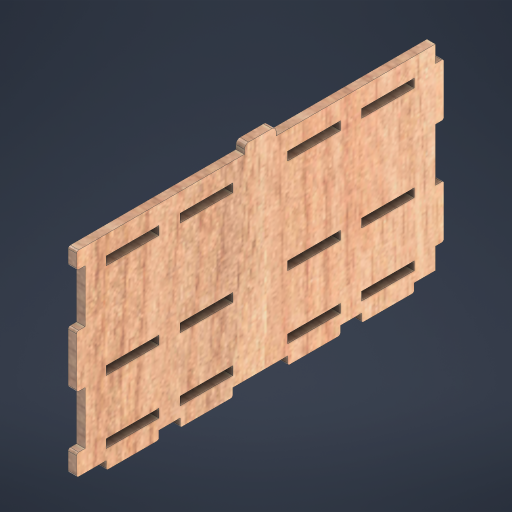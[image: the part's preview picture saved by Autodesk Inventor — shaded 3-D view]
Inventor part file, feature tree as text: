
AUTODESK INVENTOR PART (.ipt)
format: ipt  version: 2024.1 (Build 281209000, 209)  size: 609,792 bytes
history: native  units: mm
features: extrude x1, fillet x1, sketch x1
ambient origin geometry x8: Origin, YZ Plane, XZ Plane, XY Plane, X Axis, Y Axis, Z Axis, Center Point
bodies: Solid1 (feature_tree)
feature tree (3):
  extrude  "Extrusion1"  Depth=25.0mm
  fillet  "Fillet1"  Radius=25.0mm
  sketch  "Sketch1"  dims[d0=4.0mm d1=25.0mm d2=25.0mm d3=10.0mm d4=4.0mm d5=13.0mm d14=75.0mm d15=20.0mm d17=75.0mm d18=10.0mm d20=10.0mm d22=20.0mm d24=45.0mm d25=10.0mm d27=10.0mm d29=9.0mm d30=5.0mm d31=10.0mm d32=10.0mm d33=25.0mm d34=25.0mm d35=25.0mm d36=10.0mm d37=20.0mm d39=9.0mm d40=10.0mm d42=10.0mm d44=4.0mm d45=0.0mm d46=15.0mm d47=4.0mm d48=2.0mm d49=2.0mm d50=1.0mm]
